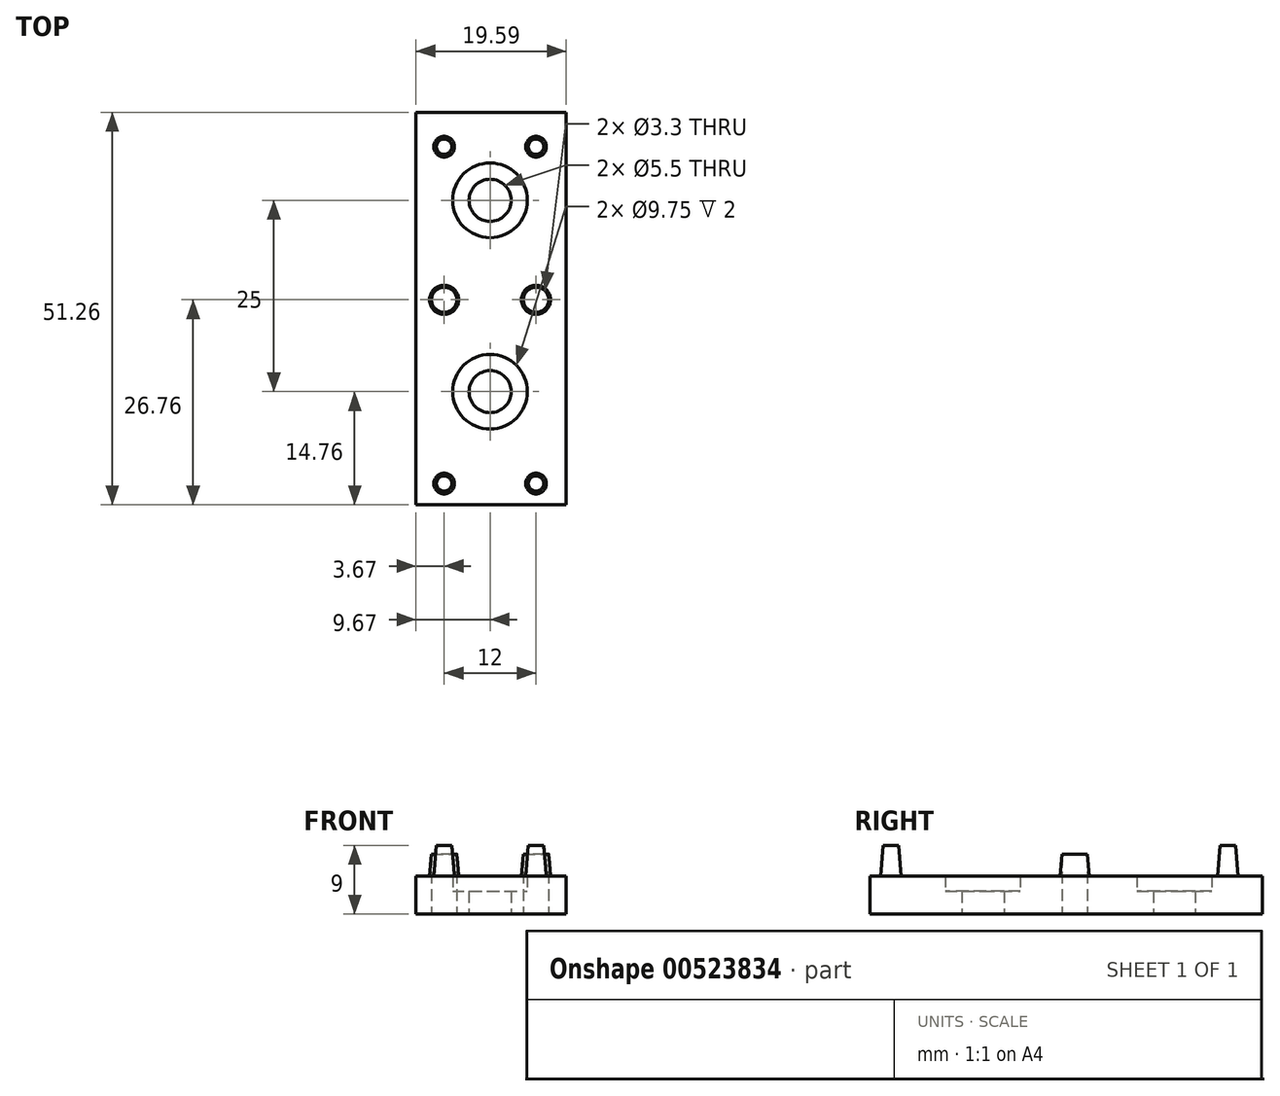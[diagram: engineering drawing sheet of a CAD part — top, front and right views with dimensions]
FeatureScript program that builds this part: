
annotation { "Feature Type Name" : "Feature", "Feature Type Description" : "" }
export const myFeature = defineFeature(function(context is Context, id is Id, definition is map)
    precondition{}
    {
        {
            var Q0;
            Q0=qCreatedBy(makeId("Top.planeOp"),FACE);
            var sketch = newSketch(context, id + "F0", { "sketchPlane" : qUnion([Q0])});
            skLineSegment(sketch, "E0.top", {"start": v(6, -12) * mm, "end": v(-6, -12) * mm, "construction": true});
            skLineSegment(sketch, "E0.left", {"start": v(6, 12) * mm, "end": v(6, -12) * mm, "construction": true});
            skLineSegment(sketch, "E0.right", {"start": v(-6, 12) * mm, "end": v(-6, -12) * mm, "construction": true});
            skPoint(sketch, "E0.middle", {"position": v(0, 0) * mm});
            skLineSegment(sketch, "E1", {"start": v(6, 12) * mm, "end": v(6, 32) * mm, "construction": true});
            skPoint(sketch, "E2", {"position": v(6, 32) * mm});
            skPoint(sketch, "E3", {"position": v(-6, 32) * mm});
            skSolve(sketch);
        }
        {
            var Q0;
            Q0=qCreatedBy(makeId("Top.planeOp"),FACE);
            var sketch = newSketch(context, id + "F1", { "sketchPlane" : qUnion([Q0])});
            skPoint(sketch, "E4.middle", {"position": v(0, 0) * mm});
            skLineSegment(sketch, "E5.bottom", {"start": v(9.92, -14.76) * mm, "end": v(-9.67, -14.76) * mm});
            skLineSegment(sketch, "E5.top", {"start": v(9.92, 36.5) * mm, "end": v(-9.67, 36.5) * mm});
            skLineSegment(sketch, "E5.left", {"start": v(9.92, -14.76) * mm, "end": v(9.92, 36.5) * mm});
            skLineSegment(sketch, "E5.right", {"start": v(-9.67, -14.76) * mm, "end": v(-9.67, 36.5) * mm});
            skSolve(sketch);
        }
        {
            var Q0;
            Q0=makeQuery(id+"F1.imprint","IMPRINT",FACE,{"disambiguationData":[TD([[makeQuery(id+"F1.imprint","IMPRINT",EDGE,{"derivedFrom":sQuery(id+"F1.wireOp",EDGE,"E4.bottom")}),1.0]])]});
            var Q1;
            Q1=makeQuery(id+"F1.imprint","IMPRINT",FACE,{"disambiguationData":[TD([[makeQuery(id+"F1.imprint","IMPRINT",EDGE,{"derivedFrom":sQuery(id+"F1.wireOp",EDGE,"E5.bottom")}),-1.0]])]});
            extrude(context, id + "F2", {"entities" : qUnion([Q0, Q1]), "oppositeDirection" : true, "depth" : 5 * mm, "offsetDistance" : 25 * mm});
        }
        {
            var Q0;
            Q0=makeQuery(id+"F2.opExtrude","CAP_FACE",FACE,{"disambiguationData":[OSD([sQuery(id+"F1.wireOp",EDGE,"E5.bottom"),sQuery(id+"F1.wireOp",EDGE,"E5.top"),sQuery(id+"F1.wireOp",EDGE,"E5.left"),sQuery(id+"F1.wireOp",EDGE,"E5.right")])],"isStart":true});
            var sketch = newSketch(context, id + "F3", { "sketchPlane" : qUnion([Q0])});
            skCircle(sketch, "E6", {"center": v(-6, 32) * mm, "radius": 1.35 * mm});
            skCircle(sketch, "E7", {"center": v(6, 32) * mm, "radius": 1.35 * mm});
            skCircle(sketch, "E8", {"center": v(6, 12) * mm, "radius": 1.9 * mm});
            skCircle(sketch, "E9", {"center": v(-6, 12) * mm, "radius": 1.9 * mm});
            skCircle(sketch, "E10", {"center": v(6, -12) * mm, "radius": 1.35 * mm});
            skCircle(sketch, "E11", {"center": v(-6, -12) * mm, "radius": 1.35 * mm});
            skSolve(sketch);
        }
        {
            var Q0;
            Q0 = qSketchRegion(id + "F3", true);
            extrude(context, id + "F4", {"entities" : qUnion([Q0]), "operationType" : NewBodyOperationType.ADD, "depth" : 4 * mm, "offsetDistance" : 25 * mm, "hasDraft" : true, "draftAngle" : 5 * degree, "draftPullDirection" : true});
        }
        {
            var Q0;
            Q0=sQuery(id+"F0.wireOp",VERTEX,"E0.right.start");
            var Q1;
            Q1=sQuery(id+"F0.wireOp",VERTEX,"E1.start");
            var Q2;
            Q2=makeQuery(id+"F2.opExtrude","SWEPT_BODY",BODY,{"disambiguationData":[OSD([sQuery(id+"F1.wireOp",EDGE,"E5.bottom"),sQuery(id+"F1.wireOp",EDGE,"E5.top"),sQuery(id+"F1.wireOp",EDGE,"E5.left"),sQuery(id+"F1.wireOp",EDGE,"E5.right")])]});
            hole(context, id + "F5", {"style" : HoleStyle.SIMPLE, "endStyle" : HoleEndStyle.BLIND, "oppositeDirection" : true, "holeDiameter" : 3 * mm, "holeDepth" : 25 * mm, "isTappedThrough" : true, "tappedDepth" : 12 * mm, "tapClearance" : 3, "startFromSketch" : true, "locations" : qUnion([Q0, Q1]), "scope" : qUnion([Q2])});
        }
        {
            var Q0;
            Q0=sQuery(id+"F0.wireOp",VERTEX,"E1.start");
            var Q1;
            Q1=sQuery(id+"F0.wireOp",VERTEX,"E0.right.start");
            var Q2;
            Q2=makeQuery(id+"F2.opExtrude","SWEPT_BODY",BODY,{"disambiguationData":[OSD([sQuery(id+"F1.wireOp",EDGE,"E5.bottom"),sQuery(id+"F1.wireOp",EDGE,"E5.top"),sQuery(id+"F1.wireOp",EDGE,"E5.left"),sQuery(id+"F1.wireOp",EDGE,"E5.right")])]});
            hole(context, id + "F6", {"style" : HoleStyle.SIMPLE, "endStyle" : HoleEndStyle.BLIND, "standardTappedOrClearance" : lookupTablePath({ "standard" : "ISO", "fit" : "Normal", "size" : "M3", "type" : "Clearance" }), "standardBlindInLast" : lookupTablePath({ "fit" : "Standard", "standard" : "ISO", "size" : "M3", "type" : "Clearance" }), "holeDiameter" : 3.3 * mm, "holeDepth" : 25 * mm, "isTappedThrough" : true, "tappedDepth" : 12 * mm, "tapClearance" : 3, "startFromSketch" : true, "locations" : qUnion([Q0, Q1]), "scope" : qUnion([Q2])});
        }
        {
            var Q0;
            Q0=makeQuery(id+"F2.opExtrude","CAP_FACE",FACE,{"disambiguationData":[OSD([sQuery(id+"F1.wireOp",EDGE,"E5.bottom"),sQuery(id+"F1.wireOp",EDGE,"E5.top"),sQuery(id+"F1.wireOp",EDGE,"E5.left"),sQuery(id+"F1.wireOp",EDGE,"E5.right")])],"isStart":true});
            var sketch = newSketch(context, id + "F7", { "sketchPlane" : qUnion([Q0])});
            skPoint(sketch, "E12", {"position": v(0, 0) * mm});
            skPoint(sketch, "E13", {"position": v(0, 25) * mm});
            skSolve(sketch);
        }
        {
            var Q0;
            Q0=sQuery(id+"F7.wireOp",VERTEX,"E12");
            var Q1;
            Q1=sQuery(id+"F7.wireOp",VERTEX,"E13");
            var Q2;
            Q2=makeQuery(id+"F2.opExtrude","SWEPT_BODY",BODY,{"disambiguationData":[OSD([sQuery(id+"F1.wireOp",EDGE,"E5.bottom"),sQuery(id+"F1.wireOp",EDGE,"E5.top"),sQuery(id+"F1.wireOp",EDGE,"E5.left"),sQuery(id+"F1.wireOp",EDGE,"E5.right")])]});
            hole(context, id + "F8", {"style" : HoleStyle.C_BORE, "endStyle" : HoleEndStyle.BLIND, "holeDiameter" : 5.5 * mm, "cBoreDiameter" : 9.75 * mm, "cBoreDepth" : 2 * mm, "holeDepth" : 25 * mm, "isTappedThrough" : true, "tappedDepth" : 12 * mm, "tapClearance" : 3, "startFromSketch" : true, "locations" : qUnion([Q0, Q1]), "scope" : qUnion([Q2])});
        }
    });
